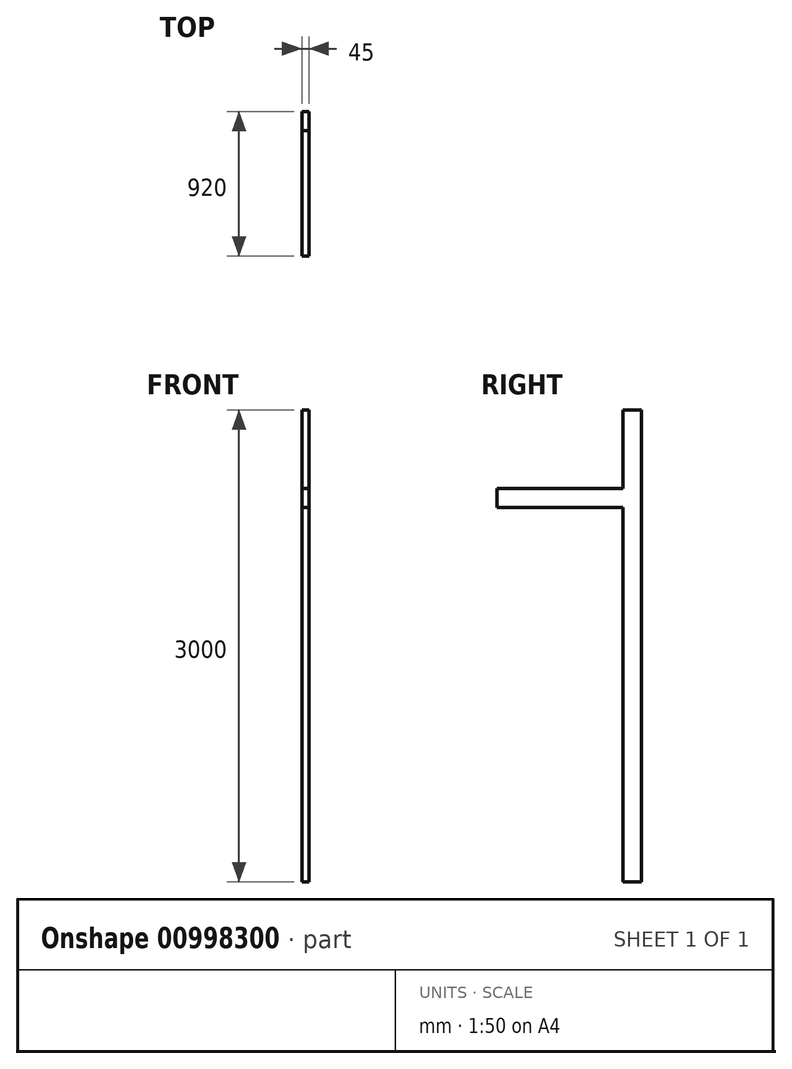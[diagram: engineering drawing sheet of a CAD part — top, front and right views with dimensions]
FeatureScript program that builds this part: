
annotation { "Feature Type Name" : "Feature", "Feature Type Description" : "" }
export const myFeature = defineFeature(function(context is Context, id is Id, definition is map)
    precondition{}
    {
        {
            var Q0;
            Q0=qCreatedBy(makeId("Front.planeOp"),FACE);
            var sketch = newSketch(context, id + "F0", { "sketchPlane" : qUnion([Q0])});
            skLineSegment(sketch, "E0.bottom", {"start": v(0, 0) * mm, "end": v(45, 0) * mm});
            skLineSegment(sketch, "E0.top", {"start": v(0, -120) * mm, "end": v(45, -120) * mm});
            skLineSegment(sketch, "E0.left", {"start": v(0, 0) * mm, "end": v(0, -120) * mm});
            skLineSegment(sketch, "E0.right", {"start": v(45, 0) * mm, "end": v(45, -120) * mm});
            skSolve(sketch);
        }
        {
            var Q0;
            Q0=makeQuery(id+"F0.imprint","IMPRINT",FACE,{"disambiguationData":[TD([[makeQuery(id+"F0.imprint","IMPRINT",EDGE,{"derivedFrom":sQuery(id+"F0.wireOp",EDGE,"E0.bottom")}),-1.0]])]});
            extrude(context, id + "F1", {"entities" : qUnion([Q0]), "depth" : 800 * mm, "offsetDistance" : 25 * mm});
        }
        {
            var Q0;
            Q0=qCreatedBy(makeId("Top.planeOp"),FACE);
            var sketch = newSketch(context, id + "F2", { "sketchPlane" : qUnion([Q0])});
            skLineSegment(sketch, "E1.left", {"start": v(0, 0) * mm, "end": v(0, 0) * mm});
            skLineSegment(sketch, "E2.left", {"start": v(48, 130.56) * mm, "end": v(48, 130.44) * mm});
            skLineSegment(sketch, "E2.right", {"start": v(0, 130.56) * mm, "end": v(0, 130.44) * mm});
            skLineSegment(sketch, "E3.bottom", {"start": v(0, 0) * mm, "end": v(45, 0) * mm});
            skLineSegment(sketch, "E3.top", {"start": v(0, 120) * mm, "end": v(45, 120) * mm});
            skLineSegment(sketch, "E3.left", {"start": v(0, 0) * mm, "end": v(0, 120) * mm});
            skLineSegment(sketch, "E3.right", {"start": v(45, 0) * mm, "end": v(45, 120) * mm});
            skSolve(sketch);
        }
        {
            var Q0;
            Q0=makeQuery(id+"F2.imprint","IMPRINT",FACE,{"disambiguationData":[TD([[makeQuery(id+"F2.imprint","IMPRINT",EDGE,{"derivedFrom":sQuery(id+"F2.wireOp",EDGE,"E3.bottom")}),1.0]])]});
            extrude(context, id + "F3", {"entities" : qUnion([Q0]), "operationType" : NewBodyOperationType.ADD, "depth" : 500 * mm, "offsetDistance" : 25 * mm, "hasSecondDirection" : true, "secondDirectionOppositeDirection" : true, "secondDirectionDepth" : 2500 * mm});
        }
    });
